# Revit family: legrand boites de sol version standard FR
name_source: partatom
category: Installations électriques
units: mm (PartAtom-declared; Revit-internal decimal feet)

## family parameters
Conserver l'orientation des annotations = Non
Cote de connecteur circulaire = Utiliser le diamètre
Couper avec des vides une fois chargée = Non
Hôte = Face
Partagée = Non
Point de calcul de pièce = Non
Type d'élément = Normal

## types (9) — shared parameters
00 = Reservation boitier : 00
000000 = Accessoire : Aucun
01 = Reservation boitier : 01
02 = Reservation boitier : 02
088000 = Couvercle : 088000
088001 = Couvercle : 088001
088002 = Couvercle : 088002
088003 = Couvercle : 088003
088004 = Couvercle : 088004
088005 = Couvercle : 088005
088006 = Couvercle : 088006
088007 = Couvercle : 088007
088008 = Couvercle : 088008
088015 = Plaque finition : 088015
088016 = Plaque finition : 088016
088017 = Plaque finition : 088017
088026 = Accessoire : 088026
088027 = Accessoire : 088027
088028 = Accessoire : 088028
088045 = Plaque finition : 088045
088046 = Plaque finition : 088046
088047 = Plaque finition : 088047
088048 = Plaque finition : 088048
088049 = Plaque finition : 088049
088050 = Plaque finition : 088050
088080 = Boitier d'encastrement : 088080
088081 = Accessoire : 088081
088082 = Accessoire : 088082
088083 = Accessoire : 088083
088086 = Accessoire : 088086 + 088088
088086-2 = Accessoire : 088086 + (2x088088)
088090 = Boitier d'encastrement : 088090
088091 = Boitier d'encastrement : 088091
088092 = Boitier d'encastrement : 088092
26 = Reservation boitier : 26
27 = Reservation boitier : 27
28 = Reservation boitier : 28
80 = Reservation boitier : 80
90 = Reservation boitier : 90
91 = Reservation boitier : 91
92 = Reservation boitier : 92
Auto = Type de sol utilisé : Auto ajustable
Brass = Finition : Laiton
Fabricant = LEGRAND
Inox = Finition : Acier inoxydable
Plastic = Finition : Gris RAL 7031
StdB125 = Type de sol utilisé : Plancher béton inférieur 125 mm
StdB170 = Type de sol utilisé : Plancher béton entre 125 mm et 170 mm
StdB250 = Type de sol utilisé : Plancher béton entre 170 mm et 250 mm
StdT = Type de sol utilisé : Plancher technique
zero-valued in all types: Elévation par défaut

## per-type parameters (varying)
| type | Description | Support | Support appareillage | Supports |
| 8 modules 2x4 | Boite de sol universelle standard 8 modules vertical | 23 | Support appareillage : 088023 | 088023 |
| 12 modules 2x6 | Boite de sol universelle standard 12 modules vertical | 24 | Support appareillage : 088024 | 088024 |
| 16 modules 2x8 | Boite de sol universelle standard 16 modules vertical | 25 | Support appareillage : 088025 | 088025 |
| 12 modules 3x4 | Boite de sol universelle standard 12 modules horizontal ajustable | 20 | Support appareillage : 088020 | 088020 |
| 18 modules 3x6 | Boite de sol universelle standard 18 modules horizontal ajustable | 21 | Support appareillage : 088021 | 088021 |
| 24 modules 3x8 | Boite de sol universelle standard 24 modules horizontal ajustable | 22 | Support appareillage : 088022 | 088022 |
| Trappe de visite 8-12 modules | Trappe de visite couvercle standard 8/12 modules | 39 | Support appareillage : 088039 | 088039 |
| Trappe de visite 12-18 modules | Trappe de visite couvercle standard 12/18 modules | 40 | Support appareillage : 088040 | 088040 |
| Trappe de visite 16-24 modules | Trappe de visite couvercle standard 16/24 modules | 41 | Support appareillage : 088041 | 088041 |
